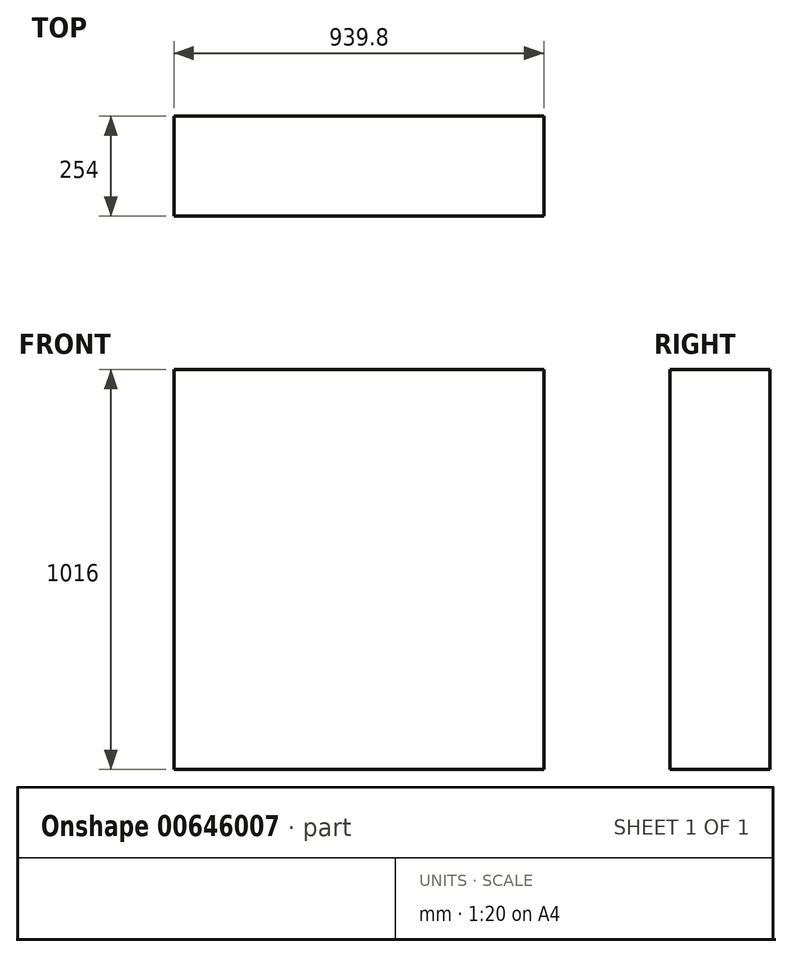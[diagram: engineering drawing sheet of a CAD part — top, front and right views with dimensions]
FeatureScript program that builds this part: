
annotation { "Feature Type Name" : "Feature", "Feature Type Description" : "" }
export const myFeature = defineFeature(function(context is Context, id is Id, definition is map)
    precondition{}
    {
        {
            var Q0;
            Q0=qCreatedBy(makeId("Top.planeOp"),FACE);
            var sketch = newSketch(context, id + "F0", { "sketchPlane" : qUnion([Q0])});
            skLineSegment(sketch, "E0.bottom", {"start": v(0, 0) * mm, "end": v(-939.8, 0) * mm});
            skLineSegment(sketch, "E0.top", {"start": v(0, -254) * mm, "end": v(-939.8, -254) * mm});
            skLineSegment(sketch, "E0.left", {"start": v(0, 0) * mm, "end": v(0, -254) * mm});
            skLineSegment(sketch, "E0.right", {"start": v(-939.8, 0) * mm, "end": v(-939.8, -254) * mm});
            skSolve(sketch);
        }
        {
            var Q0;
            Q0=makeQuery(id+"F0.imprint","IMPRINT",FACE,{"disambiguationData":[TD([[makeQuery(id+"F0.imprint","IMPRINT",EDGE,{"derivedFrom":sQuery(id+"F0.wireOp",EDGE,"E0.bottom")}),1.0]])]});
            extrude(context, id + "F1", {"entities" : qUnion([Q0]), "depth" : 1016 * mm, "offsetDistance" : 25.4 * mm});
        }
    });
